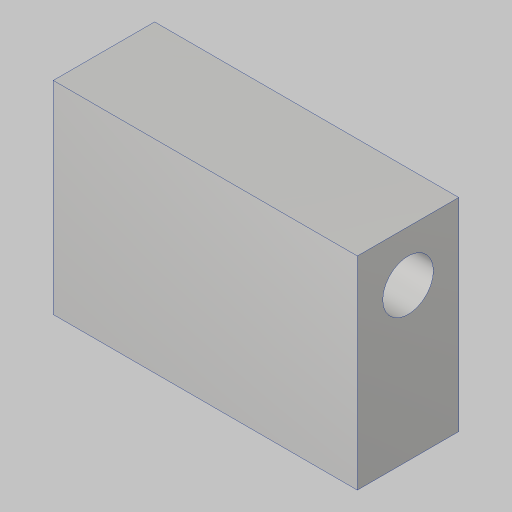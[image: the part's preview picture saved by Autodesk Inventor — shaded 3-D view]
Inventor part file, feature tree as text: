
AUTODESK INVENTOR PART (.ipt)
format: ipt  version: 2023.5 (Build 275446000, 446)  size: 118,784 bytes
history: native  units: in
note: dims shown in document units (in); Inventor stores cm internally (conversion verified against a paired STEP export)
features: sketch x3, hole x2, extrude x1
ambient origin geometry x8: Origin, YZ Plane, XZ Plane, XY Plane, X Axis, Y Axis, Z Axis, Center Point
bodies: Solid1 (feature_tree)
feature tree (6):
  extrude  "Extrusion1"  Depth=1.0in
  hole  "Hole1"  [1 undecoded]
  hole  "Hole2"  [1 undecoded]
  sketch  "Sketch1"  dims[d0=2.0in d1=1.0in]
  sketch  "Sketch2"  dims[d2=3.0in d3=0.0in d4=0.5in]
  sketch  "Sketch3"  dims[d5=0.5in d6=0.75in d7=0.385in d8=0.25in d9=0.5635in d10=1.0in d11=0.8108in d12=2.0in d13=0.156in d14=0.38in d15=0.375in d16=0.25in d17=0.5635in d18=1.0in d19=0.8108in]
note: 2 required parameter values undecoded (feature->parameter linkage not recoverable at this tier; creation-order binding heuristic only, values carry confidence <= 0.55)
